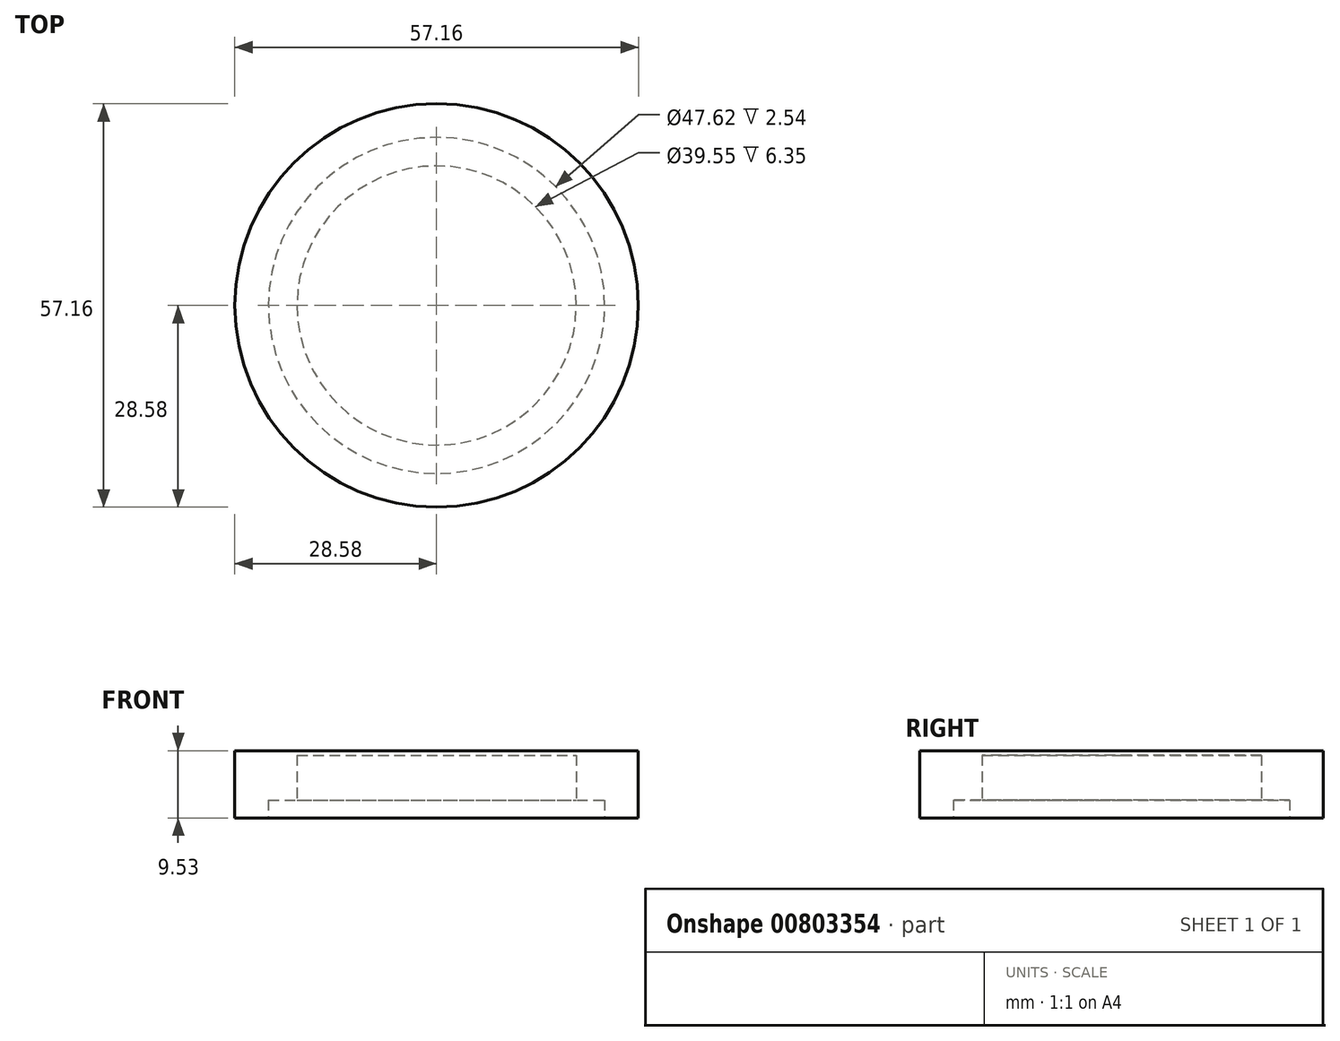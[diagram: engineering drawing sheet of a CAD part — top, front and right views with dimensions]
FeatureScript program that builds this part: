
annotation { "Feature Type Name" : "Feature", "Feature Type Description" : "" }
export const myFeature = defineFeature(function(context is Context, id is Id, definition is map)
    precondition{}
    {
        {
            var Q0;
            Q0=qCreatedBy(makeId("Top.planeOp"),FACE);
            var sketch = newSketch(context, id + "F0", { "sketchPlane" : qUnion([Q0])});
            skCircle(sketch, "E0", {"center": v(0, 0) * mm, "radius": 28.58 * mm});
            skSolve(sketch);
        }
        {
            var Q0;
            Q0 = qSketchRegion(id + "F0", true);
            extrude(context, id + "F1", {"entities" : qUnion([Q0]), "depth" : 9.52 * mm, "offsetDistance" : 25.4 * mm});
        }
        {
            var Q0;
            Q0=makeQuery(id+"F1.opExtrude","CAP_FACE",FACE,{"disambiguationData":[OSD([sQuery(id+"F0.wireOp",EDGE,"E0")])],"isStart":true});
            var sketch = newSketch(context, id + "F2", { "sketchPlane" : qUnion([Q0])});
            skCircle(sketch, "E1", {"center": v(0, 0) * mm, "radius": 23.81 * mm});
            skSolve(sketch);
        }
        {
            var Q0;
            Q0=makeQuery(id+"F2.imprint","IMPRINT",FACE,{"disambiguationData":[TD([[makeQuery(id+"F2.imprint","IMPRINT",EDGE,{"derivedFrom":sQuery(id+"F2.wireOp",EDGE,"E1")}),1.0]])]});
            extrude(context, id + "F3", {"entities" : qUnion([Q0]), "operationType" : NewBodyOperationType.REMOVE, "oppositeDirection" : true, "depth" : 2.54 * mm, "offsetDistance" : 25.4 * mm});
        }
        {
            var Q0;
            Q0=makeQuery(id+"F3.boolean.opBoolean","COPY",FACE,{"derivedFrom":makeQuery(id+"F3.opExtrude","CAP_FACE",FACE,{"disambiguationData":[OSD([sQuery(id+"F2.wireOp",EDGE,"E1")])],"isStart":false})});
            var sketch = newSketch(context, id + "F4", { "sketchPlane" : qUnion([Q0])});
            skCircle(sketch, "E2", {"center": v(0, 0) * mm, "radius": 19.77 * mm});
            skSolve(sketch);
        }
        {
            var Q0;
            Q0=makeQuery(id+"F4.imprint","IMPRINT",FACE,{"disambiguationData":[TD([[makeQuery(id+"F4.imprint","IMPRINT",EDGE,{"derivedFrom":sQuery(id+"F4.wireOp",EDGE,"E2")}),1.0]])]});
            extrude(context, id + "F5", {"entities" : qUnion([Q0]), "operationType" : NewBodyOperationType.REMOVE, "oppositeDirection" : true, "depth" : 6.35 * mm, "offsetDistance" : 25.4 * mm});
        }
    });
